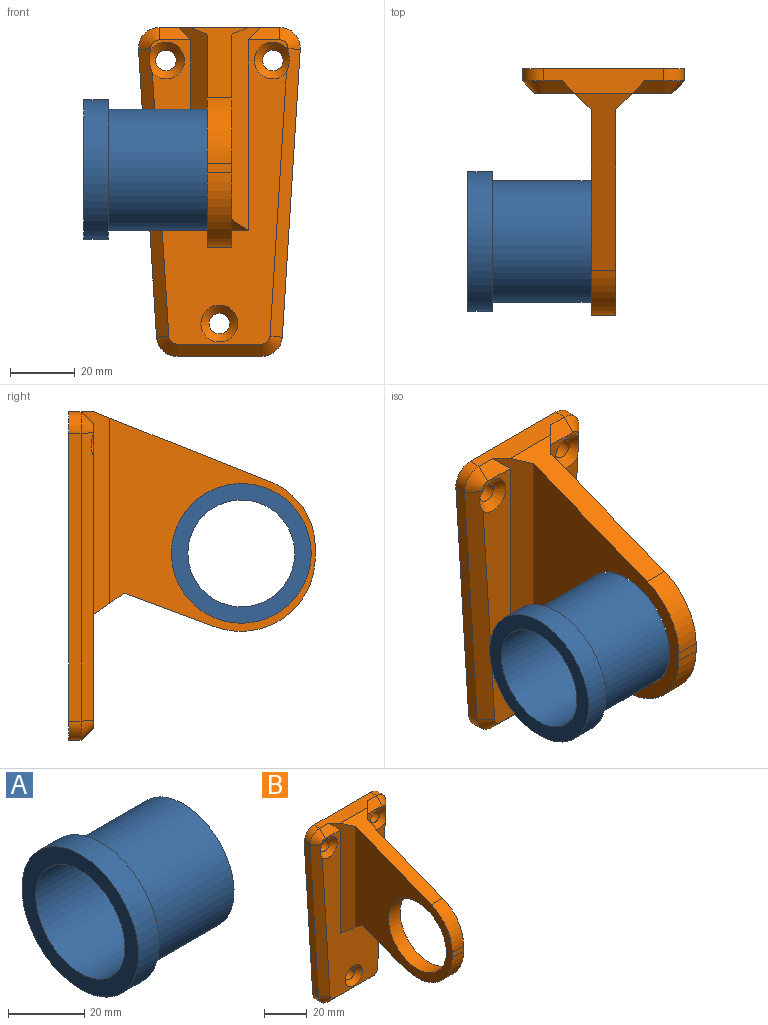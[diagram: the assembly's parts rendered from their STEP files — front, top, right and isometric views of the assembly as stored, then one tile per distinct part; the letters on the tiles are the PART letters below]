
ASSEMBLY  parts=2 mates=1
PART A: 6 faces, bbox 38.1x43.2x43.2 mm
  f0: cylinder r=16.51mm len=38.1mm, axis (-1,0,0), area 3952.3mm2, adj f2,f3
  f1: cylinder r=18.8mm len=37.59mm, axis (-1,0,0), area 3599.6mm2, adj f2,f5
  f2: plane 37.59x37.59mm, normal (1,0,0), area 253.6mm2, adj f0,f1
  f3: plane 43.18x43.18mm, normal (-1,0,0), area 608mm2, adj f0,f4
  f4: cylinder r=21.59mm len=43.18mm, axis (-1,0,0), area 1033.7mm2, adj f3,f5
  f5: plane 43.18x43.18mm, normal (1,0,0), area 354.5mm2, adj f1,f4
PART B: 36 faces, bbox 50x76.2x101.6 mm
  f0: plane 26.17x3.81mm, normal (0,0,-1), area 99.7mm2, adj f1,f10,f12,f26
  f1: cylinder r=6.35mm len=6.34mm, axis (0,1,0), area 36.5mm2, adj f0,f2,f12,f25
  f2: plane 88.9x5.56mm, normal (1,0,-0.06), area 339.4mm2, adj f1,f3,f12,f24
  f3: cylinder r=6.35mm len=6.75mm, axis (0,1,0), area 39.5mm2, adj f2,f4,f12,f23
  f4: plane 37.28x7.62mm, normal (0,0,1), area 224.3mm2, adj f3,f5,f12,f17,f19,f20,f22,f30
  f5: cylinder r=6.35mm len=6.75mm, axis (0,1,0), area 39.5mm2, adj f4,f6,f12,f29
  f6: plane 88.9x5.56mm, normal (-1,0,-0.06), area 339.4mm2, adj f5,f10,f12,f28
  f7: cylinder r=3.17mm len=6.33mm, axis (0,1,0), area 101mm2, adj f12,f33
  f8: cylinder r=3.17mm len=6.33mm, axis (0,1,0), area 101mm2, adj f12,f32
  f9: cylinder r=3.17mm len=6.33mm, axis (0,1,0), area 101mm2, adj f12,f31
  f10: cylinder r=6.35mm len=6.34mm, axis (0,1,0), area 36.5mm2, adj f0,f6,f12,f27
  f11: plane 93.98x42.36mm, normal (0,-1,0), area 2112.4mm2, adj f19,f20,f21,f22,f23,f24,f25,f26
  f12: plane 101.6x49.98mm, normal (0,1,0), area 4386.8mm2, adj f0,f1,f2,f3,f4,f5,f6,f7
  f13: plane 7.62x2.87mm, normal (0,-1,0), area 21.9mm2, adj f14,f16,f18,f35
  f14: plane 65.91x63.5mm, normal (-1,0,0), area 1857.8mm2, adj f13,f15,f17,f18,f19,f21,f34,f35
  f15: plane 28.05x10.39mm, normal (0,0.35,-0.94), area 227.9mm2, adj f14,f16,f21,f35
  f16: plane 65.91x63.5mm, normal (1,0,0), area 1857.8mm2, adj f13,f15,f17,f18,f20,f21,f34,f35
  f17: plane 54.76x21.7mm, normal (0,-0.37,0.93), area 476.6mm2, adj f4,f14,f16,f18,f19,f20
  f18: cylinder r=21.88mm len=20.34mm, axis (1,0,0), area 199mm2, adj f13,f14,f16,f17
  f19: plane 62.73x8.89mm, normal (-0.71,-0.71,0), area 441mm2, adj f4,f11,f14,f17,f21,f30
  f20: plane 62.73x8.89mm, normal (0.71,-0.71,0), area 441mm2, adj f4,f11,f16,f17,f21,f22
  f21: plane 17.78x9.53mm, normal (0,-0.57,-0.82), area 119.9mm2, adj f11,f14,f15,f16,f19,f20
  f22: plane 9.75x3.81mm, normal (0,-0.71,0.71), area 42.3mm2, adj f4,f11,f20,f23
  f23: cone r=2.54mm half-angle=45deg, axis (0,1,0), area 39.1mm2, adj f3,f11,f22,f24
  f24: plane 89.14x9.36mm, normal (0.71,-0.71,-0.04), area 475.6mm2, adj f2,f11,f23,f25,f32
  f25: cone r=2.54mm half-angle=45deg, axis (0,1,0), area 36.1mm2, adj f1,f11,f24,f26
  f26: plane 26.17x3.81mm, normal (0,-0.71,-0.71), area 141mm2, adj f0,f11,f25,f27
  f27: cone r=2.54mm half-angle=45deg, axis (0,1,0), area 36.1mm2, adj f10,f11,f26,f28
  f28: plane 89.14x9.36mm, normal (-0.71,-0.71,-0.04), area 475.6mm2, adj f6,f11,f27,f29,f33
  f29: cone r=2.54mm half-angle=45deg, axis (0,1,0), area 39.1mm2, adj f5,f11,f28,f30
  f30: plane 9.75x3.81mm, normal (0,-0.71,0.71), area 42.3mm2, adj f4,f11,f19,f29
  f31: cone r=3.17mm half-angle=45deg, axis (0,-1,0), area 100.1mm2, adj f9,f11
  f32: cone r=3.17mm half-angle=45deg, axis (0,-1,0), area 95.6mm2, adj f8,f11,f24
  f33: cone r=3.17mm half-angle=45deg, axis (0,-1,0), area 95.6mm2, adj f7,f11,f28
  f34: cylinder r=19.05mm len=38.1mm, axis (-1,0,0), area 912.1mm2, adj f14,f16
  f35: cylinder r=23.01mm len=31.01mm, axis (-1,0,0), area 337.7mm2, adj f13,f14,f15,f16
PLACE A t=(-89.57,-51.54,-6.18)mm
PLACE B t=(-47.66,1.8,-14.95)mm
MATE cylindrical A.f1 <-> B.f34  axis (-1,0,0) through (-66.71,-51.54,-6.18)mm
